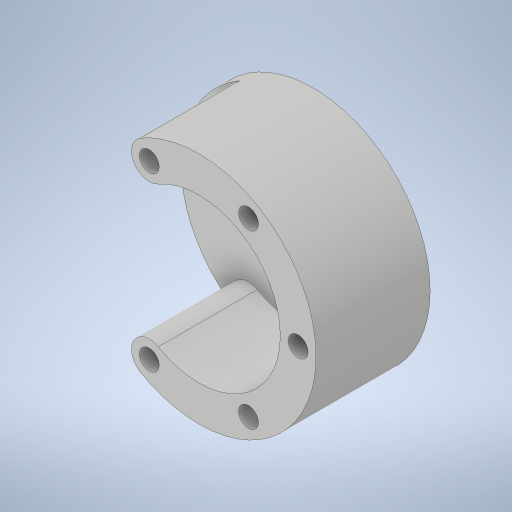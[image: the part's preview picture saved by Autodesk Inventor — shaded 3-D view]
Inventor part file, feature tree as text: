
AUTODESK INVENTOR PART (.ipt)
format: ipt  version: 2023.4 (Build 274418000, 418)  size: 269,824 bytes
history: native  units: in
note: dims shown in document units (in); Inventor stores cm internally (conversion verified against a paired STEP export)
features: sketch x3, extrude x2, hole x1
ambient origin geometry x8: Origin, YZ Plane, XZ Plane, XY Plane, X Axis, Y Axis, Z Axis, Center Point
bodies: Solid1 (feature_tree)
feature tree (6):
  extrude  "Extrusion1"  Depth=2.0in
  extrude  "Extrusion2"  Depth=2.3622in TaperAngle=360.0deg
  hole  "Hole1"  [1 undecoded]
  sketch  "Sketch1"  dims[d0=2.36in d1=2.0in]
  sketch  "Sketch2"  dims[d2=0.201in d3=2.3622in d5=360.0deg]
  sketch  "Sketch3"  dims[d11=1.0in d12=0.0in d13=0.775in d14=2.36in d15=0.15in d16=0.0in d17=2.3622in d19=360.0deg d21=0.201in d22=0.75in d23=0.375in d24=0.25in d25=0.5635in d26=1.25in d27=0.8108in]
note: 1 required parameter value undecoded (feature->parameter linkage not recoverable at this tier; creation-order binding heuristic only, values carry confidence <= 0.55)
